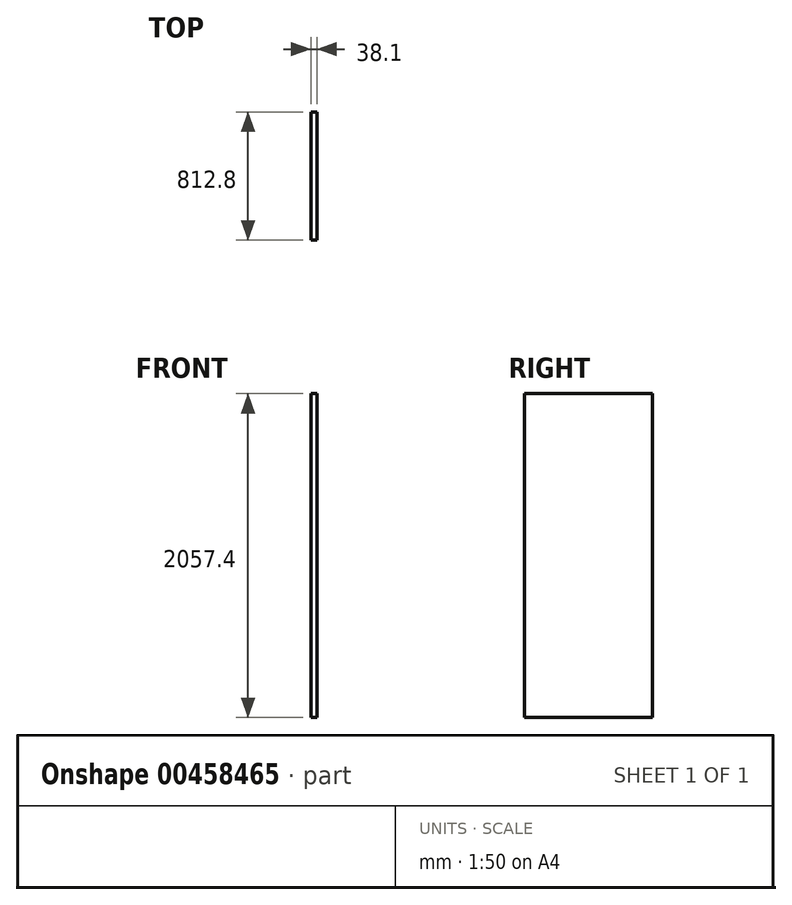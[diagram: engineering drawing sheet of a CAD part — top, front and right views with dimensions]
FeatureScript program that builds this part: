
annotation { "Feature Type Name" : "Feature", "Feature Type Description" : "" }
export const myFeature = defineFeature(function(context is Context, id is Id, definition is map)
    precondition{}
    {
        {
            var Q0;
            Q0=qCreatedBy(makeId("Right.planeOp"),FACE);
            var sketch = newSketch(context, id + "F0", { "sketchPlane" : qUnion([Q0])});
            skLineSegment(sketch, "E0.bottom", {"start": v(-494.36, -1029.5) * mm, "end": v(318.44, -1029.5) * mm});
            skLineSegment(sketch, "E0.top", {"start": v(-494.36, 1027.9) * mm, "end": v(318.44, 1027.9) * mm});
            skLineSegment(sketch, "E0.left", {"start": v(-494.36, -1029.5) * mm, "end": v(-494.36, 1027.9) * mm});
            skLineSegment(sketch, "E0.right", {"start": v(318.44, -1029.5) * mm, "end": v(318.44, 1027.9) * mm});
            skSolve(sketch);
        }
        {
            var Q0;
            Q0=makeQuery(id+"F0.imprint","IMPRINT",FACE,{"disambiguationData":[TD([[makeQuery(id+"F0.imprint","IMPRINT",EDGE,{"derivedFrom":sQuery(id+"F0.wireOp",EDGE,"E0.bottom")}),1.0]])]});
            extrude(context, id + "F1", {"entities" : qUnion([Q0]), "endBound" : BoundingType.SYMMETRIC, "depth" : 38.1 * mm});
        }
    });
